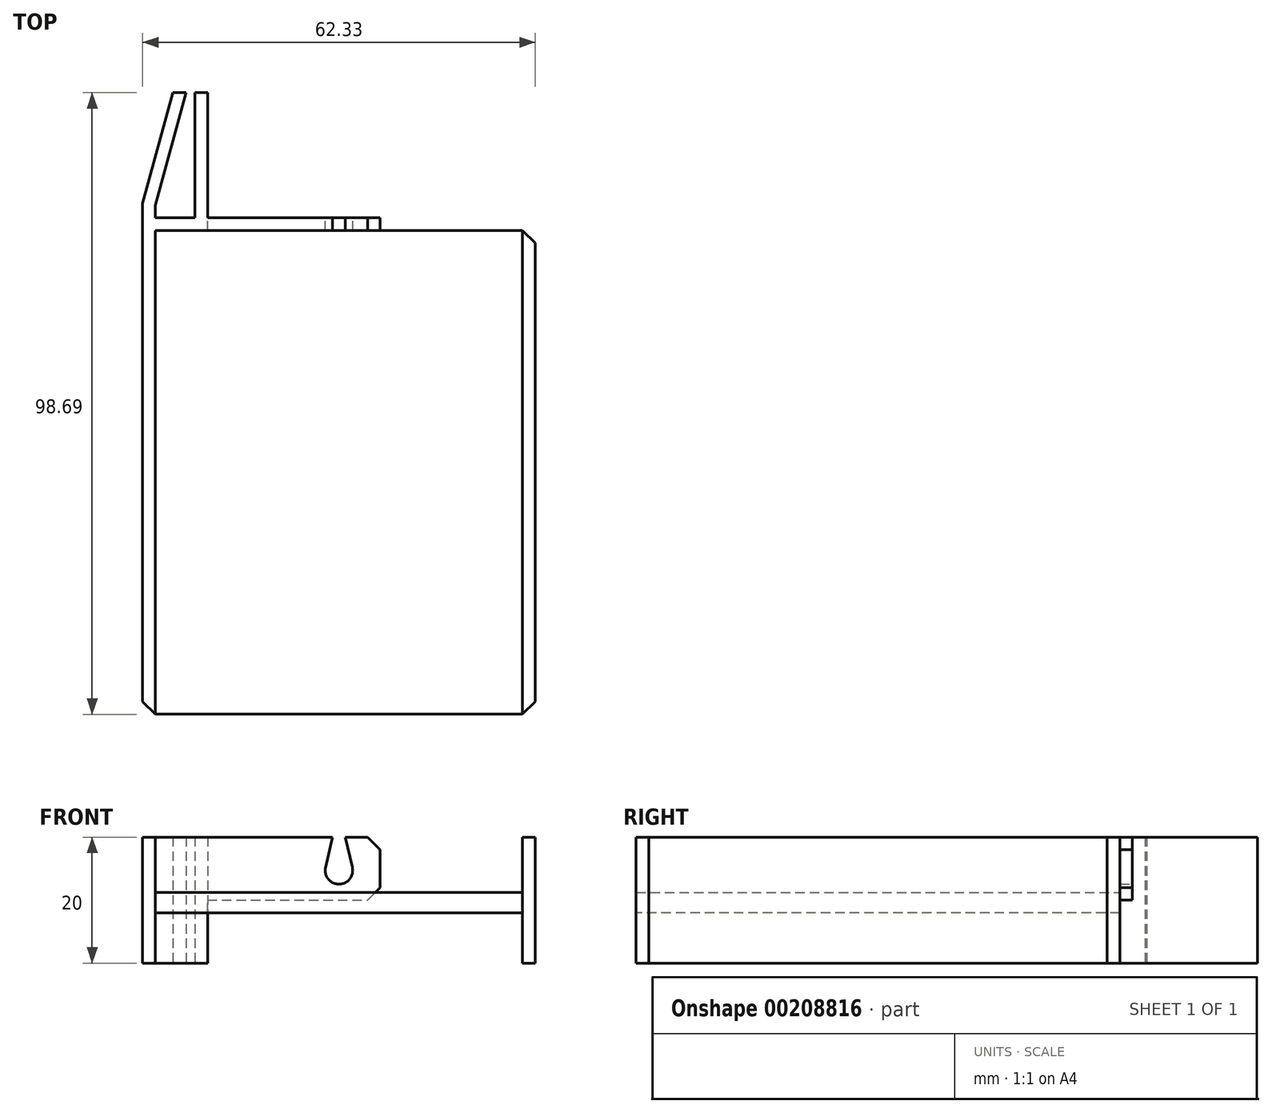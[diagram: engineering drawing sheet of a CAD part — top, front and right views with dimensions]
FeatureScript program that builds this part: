
annotation { "Feature Type Name" : "Feature", "Feature Type Description" : "" }
export const myFeature = defineFeature(function(context is Context, id is Id, definition is map)
    precondition{}
    {
        {
            var Q0;
            Q0=qCreatedBy(makeId("Top.planeOp"),FACE);
            var sketch = newSketch(context, id + "F0", { "sketchPlane" : qUnion([Q0])});
            skLineSegment(sketch, "E0", {"start": v(0, -6.6) * mm, "end": v(6.3, -6.6) * mm, "construction": true});
            skLineSegment(sketch, "E1", {"start": v(0, -6.6) * mm, "end": v(0, -4.6) * mm, "construction": true});
            skLineSegment(sketch, "E2", {"start": v(0, -4.6) * mm, "end": v(4.9, -4.6) * mm, "construction": true});
            skLineSegment(sketch, "E3", {"start": v(4.9, -4.6) * mm, "end": v(4.9, 31.1) * mm, "construction": true});
            skLineSegment(sketch, "E4", {"start": v(6.3, 33.13) * mm, "end": v(6.3, -6.6) * mm, "construction": true});
            skLineSegment(sketch, "E5", {"start": v(0, -6.6) * mm, "end": v(6.3, -6.6) * mm});
            skLineSegment(sketch, "E6", {"start": v(0, -6.6) * mm, "end": v(0, -4.6) * mm});
            skLineSegment(sketch, "E7", {"start": v(6.3, -6.6) * mm, "end": v(6.3, -4.6) * mm});
            skPoint(sketch, "E7.endSnap0", {"position": v(2.45, -4.6) * mm});
            skLineSegment(sketch, "E8", {"start": v(6.3, -4.6) * mm, "end": v(6.3, 13.25) * mm});
            skPoint(sketch, "E8.endSnap0", {"position": v(4.9, 13.25) * mm});
            skLineSegment(sketch, "E9", {"start": v(0, -4.6) * mm, "end": v(4.9, 13.25) * mm});
            skLineSegment(sketch, "E10.0", {"start": v(-2, -4.33) * mm, "end": v(2.83, 13.25) * mm});
            skLineSegment(sketch, "E10.1", {"start": v(8.3, -2.59) * mm, "end": v(8.3, 13.25) * mm});
            skLineSegment(sketch, "E10.2", {"start": v(8.3, -8.6) * mm, "end": v(8.3, -2.59) * mm});
            skLineSegment(sketch, "E10.3", {"start": v(-2, -8.6) * mm, "end": v(8.3, -8.6) * mm});
            skLineSegment(sketch, "E10.4", {"start": v(-2, -8.6) * mm, "end": v(-2, -4.33) * mm});
            skLineSegment(sketch, "E11", {"start": v(4.9, 13.25) * mm, "end": v(2.83, 13.25) * mm});
            skLineSegment(sketch, "E12", {"start": v(6.3, 13.25) * mm, "end": v(8.3, 13.25) * mm});
            skLineSegment(sketch, "E13.bottom", {"start": v(-2, -8.6) * mm, "end": v(60.33, -8.6) * mm});
            skLineSegment(sketch, "E13.top", {"start": v(-2, -85.44) * mm, "end": v(60.33, -85.44) * mm});
            skLineSegment(sketch, "E13.left", {"start": v(-2, -8.6) * mm, "end": v(-2, -85.44) * mm});
            skLineSegment(sketch, "E13.right", {"start": v(60.33, -8.6) * mm, "end": v(60.33, -85.44) * mm});
            skLineSegment(sketch, "E14", {"start": v(0, -85.44) * mm, "end": v(0, -8.6) * mm});
            skLineSegment(sketch, "E15", {"start": v(58.33, -8.6) * mm, "end": v(58.33, -85.44) * mm});
            skLineSegment(sketch, "E16", {"start": v(29.16, -8.6) * mm, "end": v(29.16, -6.6) * mm});
            skLineSegment(sketch, "E17", {"start": v(29.16, -6.6) * mm, "end": v(8.3, -6.6) * mm});
            skLineSegment(sketch, "E18", {"start": v(29.16, -6.6) * mm, "end": v(35.72, -6.6) * mm});
            skLineSegment(sketch, "E19", {"start": v(35.72, -6.6) * mm, "end": v(35.72, -8.6) * mm});
            skSolve(sketch);
        }
        {
            var Q0;
            Q0=makeQuery(id+"F0.imprint","IMPRINT",FACE,{"disambiguationData":[TD([[makeQuery(id+"F0.imprint","IMPRINT",EDGE,{"derivedFrom":sQuery(id+"F0.wireOp",EDGE,"E5")}),-1.0]])]});
            extrude(context, id + "F1", {"entities" : qUnion([Q0]), "depth" : 10 * mm});
        }
        {
            var Q0;
            {var subQ6=sQuery(id+"F0.wireOp",EDGE,"E14");Q0=makeQuery(id+"F0.imprint","IMPRINT",FACE,{"disambiguationData":[TD([[makeQuery(id+"F0.imprint","IMPRINT",EDGE,{"derivedFrom":subQ6}),-1.0]])]});}
            extrude(context, id + "F2", {"entities" : qUnion([Q0]), "operationType" : NewBodyOperationType.ADD, "depth" : 1.2 * mm});
        }
        {
            var Q0;
            {var subQ2=sQuery(id+"F0.wireOp",EDGE,"E13.left");Q0=makeQuery(id+"F0.imprint","IMPRINT",FACE,{"disambiguationData":[TD([[makeQuery(id+"F0.imprint","IMPRINT",EDGE,{"derivedFrom":subQ2}),1.0]])]});}
            var Q1;
            {var subQ0=sQuery(id+"F0.wireOp",EDGE,"E13.right");Q1=makeQuery(id+"F0.imprint","IMPRINT",FACE,{"disambiguationData":[TD([[makeQuery(id+"F0.imprint","IMPRINT",EDGE,{"derivedFrom":subQ0}),-1.0]])]});}
            var Q2;
            Q2=makeQuery(id+"F1.opExtrude","CAP_FACE",FACE,{"disambiguationData":[OSD([sQuery(id+"F0.wireOp",EDGE,"E5"),sQuery(id+"F0.wireOp",EDGE,"E6"),sQuery(id+"F0.wireOp",EDGE,"E7"),sQuery(id+"F0.wireOp",EDGE,"E8"),sQuery(id+"F0.wireOp",EDGE,"E9"),sQuery(id+"F0.wireOp",EDGE,"E10.0"),sQuery(id+"F0.wireOp",EDGE,"E10.1"),sQuery(id+"F0.wireOp",EDGE,"E10.2"),sQuery(id+"F0.wireOp",EDGE,"E10.3"),sQuery(id+"F0.wireOp",EDGE,"E10.4"),sQuery(id+"F0.wireOp",EDGE,"E11"),sQuery(id+"F0.wireOp",EDGE,"E12")])],"isStart":false});
            extrude(context, id + "F3", {"entities" : qUnion([Q0, Q1]), "operationType" : NewBodyOperationType.ADD, "endBound" : BoundingType.UP_TO_SURFACE, "endBoundEntityFace" : qUnion([Q2]), "depth" : 25 * mm});
        }
        {
            var Q0;
            Q0=makeQuery(id+"F0.imprint","IMPRINT",FACE,{"disambiguationData":[TD([[makeQuery(id+"F0.imprint","IMPRINT",EDGE,{"derivedFrom":sQuery(id+"F0.wireOp",EDGE,"E5")}),-1.0]])]});
            var Q1;
            {var subQ4=sQuery(id+"F0.wireOp",EDGE,"E16");Q1=makeQuery(id+"F0.imprint","IMPRINT",FACE,{"disambiguationData":[TD([[makeQuery(id+"F0.imprint","IMPRINT",EDGE,{"derivedFrom":subQ4}),1.0]])]});}
            var Q2;
            {var subQ2=sQuery(id+"F0.wireOp",EDGE,"E16");Q2=makeQuery(id+"F0.imprint","IMPRINT",FACE,{"disambiguationData":[TD([[makeQuery(id+"F0.imprint","IMPRINT",EDGE,{"derivedFrom":subQ2}),-1.0]])]});}
            extrude(context, id + "F4", {"entities" : qUnion([Q0, Q1, Q2]), "depth" : 10 * mm});
        }
        {
            var Q0;
            Q0=makeQuery(id+"F4.opExtrude","SWEPT_FACE",FACE,{"disambiguationData":[OSD([sQuery(id+"F0.wireOp",EDGE,"E17"),sQuery(id+"F0.wireOp",EDGE,"E18")])]});
            var sketch = newSketch(context, id + "F5", { "sketchPlane" : qUnion([Q0])});
            skLineSegment(sketch, "E20", {"start": v(-28.16, 10) * mm, "end": v(-27.04, 5.2) * mm});
            skLineSegment(sketch, "E21", {"start": v(-30.16, 10) * mm, "end": v(-31.3, 5.2) * mm});
            skArc(sketch, "E22", {"start": v(-27.04, 5.2) * mm, "mid": v(-29.16, 2.52) * mm, "end": v(-31.3, 5.2) * mm});
            skLineSegment(sketch, "E23", {"start": v(-30.16, 10) * mm, "end": v(-28.16, 10) * mm});
            skSolve(sketch);
        }
        {
            var Q0;
            Q0=makeQuery(id+"F5.imprint","IMPRINT",FACE,{"disambiguationData":[TD([[makeQuery(id+"F5.imprint","IMPRINT",EDGE,{"derivedFrom":sQuery(id+"F5.wireOp",EDGE,"E20")}),-1.0]])]});
            extrude(context, id + "F6", {"entities" : qUnion([Q0]), "operationType" : NewBodyOperationType.REMOVE, "oppositeDirection" : true, "depth" : 25 * mm});
        }
        {
            var Q0;
            Q0=makeQuery(id+"F4.opExtrude","CAP_EDGE",EDGE,{"disambiguationData":[OSD([sQuery(id+"F0.wireOp",EDGE,"E19")])],"isStart":false});
            var Q1;
            Q1=makeQuery(id+"F4.opExtrude","CAP_EDGE",EDGE,{"disambiguationData":[OSD([sQuery(id+"F0.wireOp",EDGE,"E19")])],"isStart":true});
            chamfer(context, id + "F7", {"entities" : qUnion([Q0, Q1]), "width" : 2 * mm, "tangentPropagation" : true});
        }
        {
            var Q0;
            {var subQ6=sQuery(id+"F0.wireOp",EDGE,"E14");Q0=makeQuery(id+"F0.imprint","IMPRINT",FACE,{"disambiguationData":[TD([[makeQuery(id+"F0.imprint","IMPRINT",EDGE,{"derivedFrom":subQ6}),-1.0]])]});}
            extrude(context, id + "F8", {"entities" : qUnion([Q0]), "oppositeDirection" : true, "depth" : 2 * mm});
        }
        {
            var Q0;
            Q0=makeQuery(id+"F0.imprint","IMPRINT",FACE,{"disambiguationData":[TD([[makeQuery(id+"F0.imprint","IMPRINT",EDGE,{"derivedFrom":sQuery(id+"F0.wireOp",EDGE,"E5")}),-1.0]])]});
            var Q1;
            {var subQ2=sQuery(id+"F0.wireOp",EDGE,"E13.left");Q1=makeQuery(id+"F0.imprint","IMPRINT",FACE,{"disambiguationData":[TD([[makeQuery(id+"F0.imprint","IMPRINT",EDGE,{"derivedFrom":subQ2}),1.0]])]});}
            var Q2;
            {var subQ0=sQuery(id+"F0.wireOp",EDGE,"E13.right");Q2=makeQuery(id+"F0.imprint","IMPRINT",FACE,{"disambiguationData":[TD([[makeQuery(id+"F0.imprint","IMPRINT",EDGE,{"derivedFrom":subQ0}),-1.0]])]});}
            extrude(context, id + "F9", {"entities" : qUnion([Q0, Q1, Q2]), "operationType" : NewBodyOperationType.ADD, "oppositeDirection" : true, "depth" : 10 * mm});
        }
        {
            var Q0;
            Q0=makeQuery(id+"F3.opExtrude","SWEPT_EDGE",EDGE,{"disambiguationData":[OSD([sQuery(id+"F0.wireOp",EDGE,"E13.bottom"),sQuery(id+"F0.wireOp",EDGE,"E13.right")])]});
            var Q1;
            Q1=makeQuery(id+"F3.opExtrude","SWEPT_EDGE",EDGE,{"disambiguationData":[OSD([sQuery(id+"F0.wireOp",EDGE,"E13.top"),sQuery(id+"F0.wireOp",EDGE,"E13.right")])]});
            var Q2;
            Q2=makeQuery(id+"F3.opExtrude","SWEPT_EDGE",EDGE,{"disambiguationData":[OSD([sQuery(id+"F0.wireOp",EDGE,"E13.top"),sQuery(id+"F0.wireOp",EDGE,"E13.left")])]});
            var Q3;
            Q3=makeQuery(id+"F9.opExtrude","SWEPT_EDGE",EDGE,{"disambiguationData":[OSD([sQuery(id+"F0.wireOp",EDGE,"E13.top"),sQuery(id+"F0.wireOp",EDGE,"E13.left")])]});
            var Q4;
            Q4=makeQuery(id+"F9.opExtrude","SWEPT_EDGE",EDGE,{"disambiguationData":[OSD([sQuery(id+"F0.wireOp",EDGE,"E13.top"),sQuery(id+"F0.wireOp",EDGE,"E13.right")])]});
            var Q5;
            Q5=makeQuery(id+"F9.opExtrude","SWEPT_EDGE",EDGE,{"disambiguationData":[OSD([sQuery(id+"F0.wireOp",EDGE,"E13.bottom"),sQuery(id+"F0.wireOp",EDGE,"E13.right")])]});
            chamfer(context, id + "F10", {"entities" : qUnion([Q0, Q1, Q2, Q3, Q4, Q5]), "width" : 2 * mm, "tangentPropagation" : true});
        }
    });
